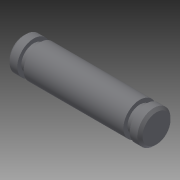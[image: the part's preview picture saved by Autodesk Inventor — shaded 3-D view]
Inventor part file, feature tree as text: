
AUTODESK INVENTOR PART (.ipt)
format: ipt  version: 2014 (Build 180170000, 170)  size: 116,224 bytes
history: native  units: in
note: dims shown in document units (in); Inventor stores cm internally (conversion verified against a paired STEP export)
features: other x21, revolve x1, sketch x1
ambient origin geometry x8: Origin, YZ Plane, XZ Plane, XY Plane, X Axis, Y Axis, Z Axis, Center Point
bodies: Solid1 (feature_tree)
feature tree (23):
  revolve  "Revolution1"  [1 undecoded]
  other  "pin_XY"
  other  "pin_YZ"
  other  "pin_ZX"
  other  "pin_X"
  other  "pin_Y"
  other  "pin_Z"
  other  "pin_Center"
  other  "rr1_XY"
  other  "rr1_YZ"
  other  "rr1_ZX"
  other  "rr1_X"
  other  "rr1_Y"
  other  "rr1_Z"
  other  "rr1_Center"
  other  "rr2_XY"
  other  "rr2_YZ"
  other  "rr2_ZX"
  other  "rr2_X"
  other  "rr2_Y"
  other  "rr2_Z"
  other  "rr2_Center"
  sketch  "Sketch_1"  dims[d0=360.0deg]
note: 1 required parameter value undecoded (feature->parameter linkage not recoverable at this tier; creation-order binding heuristic only, values carry confidence <= 0.55)
